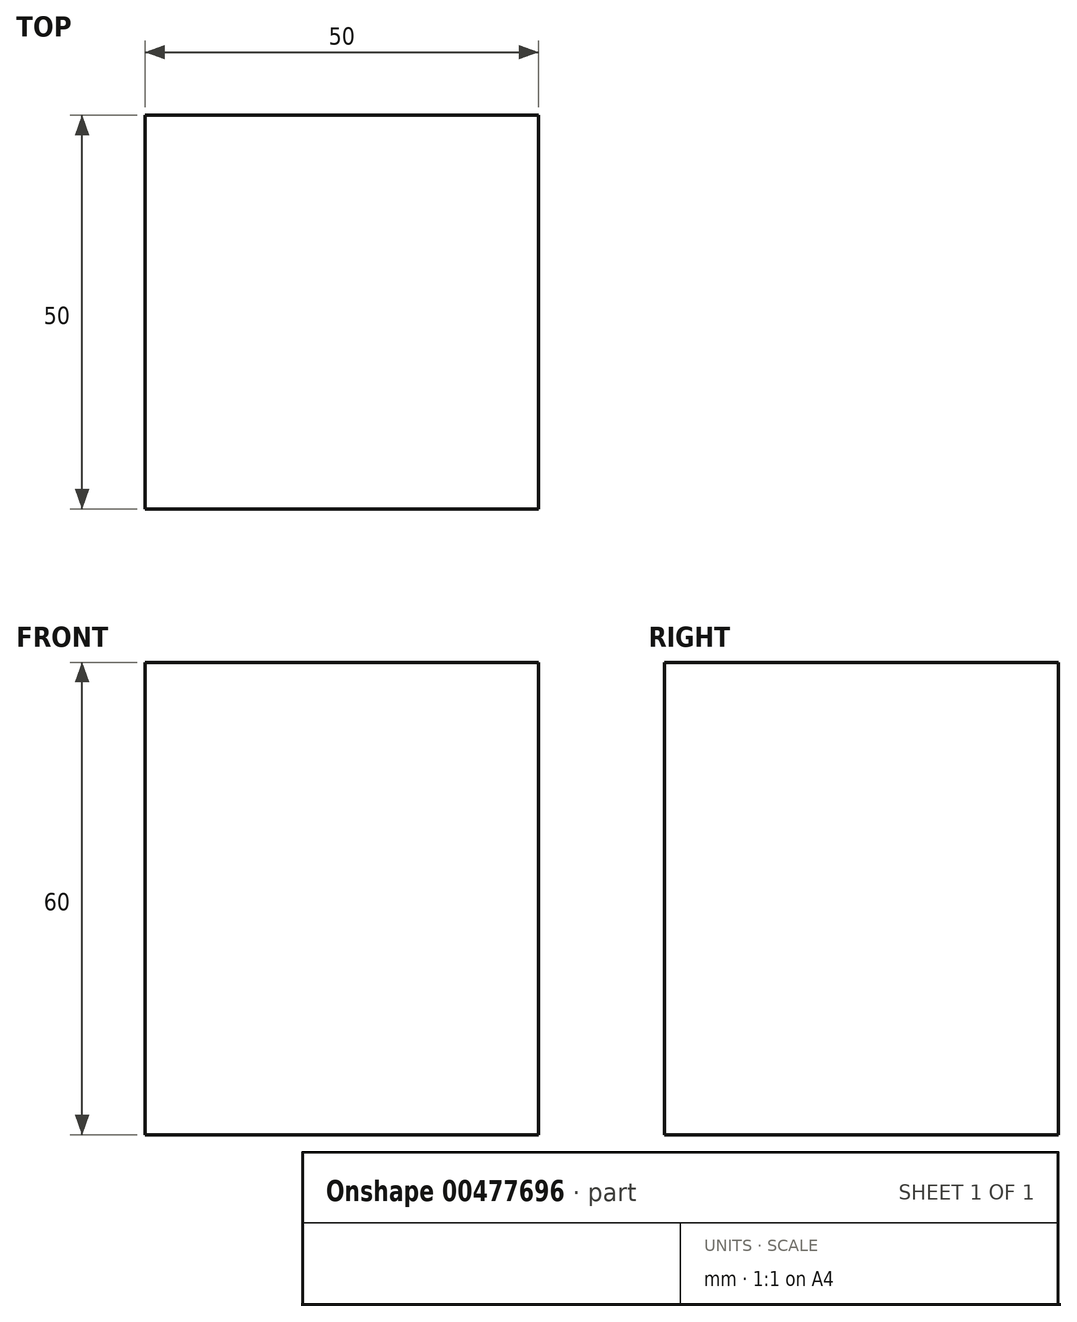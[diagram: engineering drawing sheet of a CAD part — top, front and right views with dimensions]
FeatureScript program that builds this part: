
annotation { "Feature Type Name" : "Feature", "Feature Type Description" : "" }
export const myFeature = defineFeature(function(context is Context, id is Id, definition is map)
    precondition{}
    {
        {
            var Q0;
            Q0=qCreatedBy(makeId("Top.planeOp"),FACE);
            var sketch = newSketch(context, id + "F0", { "sketchPlane" : qUnion([Q0])});
            skLineSegment(sketch, "E0.bottom", {"start": v(-15.37, 22.35) * mm, "end": v(34.63, 22.35) * mm});
            skLineSegment(sketch, "E0.top", {"start": v(-15.37, -27.65) * mm, "end": v(34.63, -27.65) * mm});
            skLineSegment(sketch, "E0.left", {"start": v(-15.37, 22.35) * mm, "end": v(-15.37, -27.65) * mm});
            skLineSegment(sketch, "E0.right", {"start": v(34.63, 22.35) * mm, "end": v(34.63, -27.65) * mm});
            skSolve(sketch);
        }
        {
            var Q0;
            Q0=makeQuery(id+"F0.imprint","IMPRINT",FACE,{"disambiguationData":[TD([[makeQuery(id+"F0.imprint","IMPRINT",EDGE,{"derivedFrom":sQuery(id+"F0.wireOp",EDGE,"E0.bottom")}),-1.0]])]});
            extrude(context, id + "F1", {"entities" : qUnion([Q0]), "depth" : 60 * mm});
        }
    });
